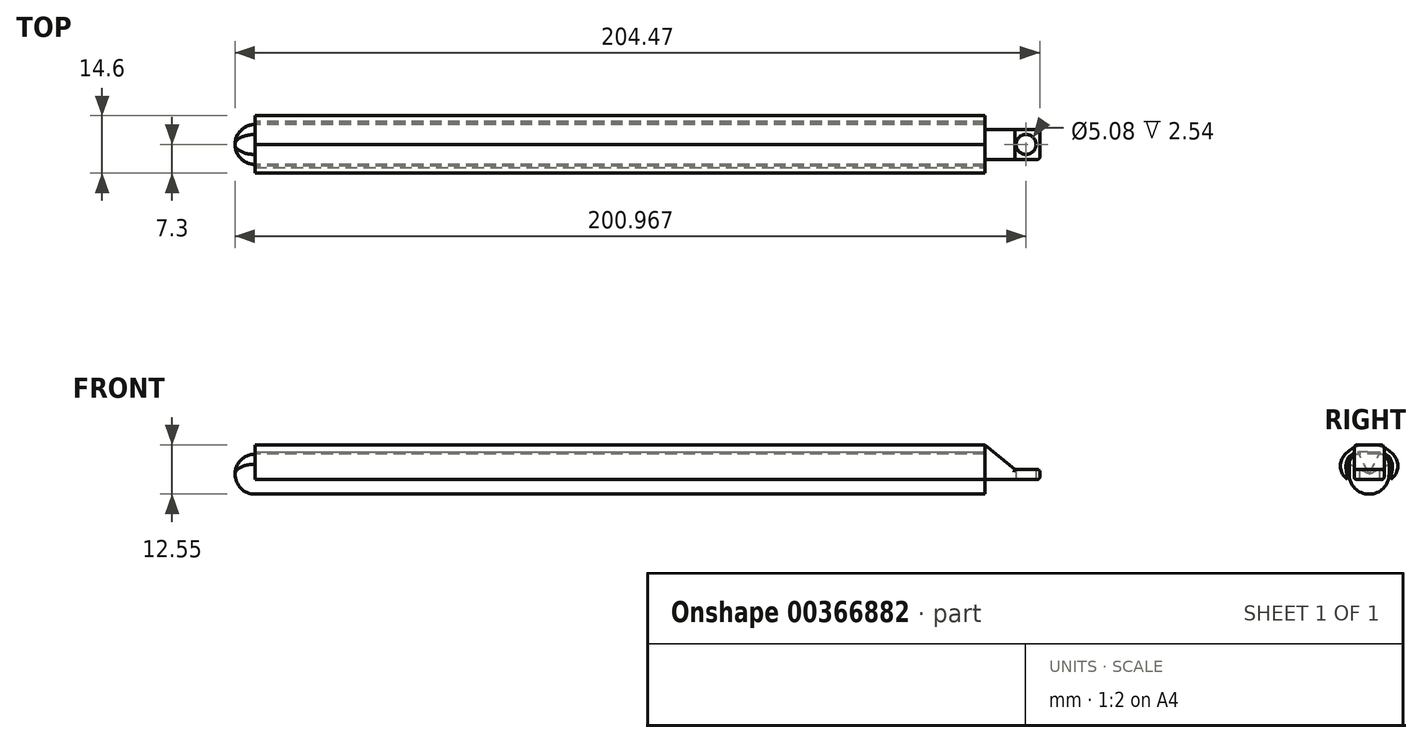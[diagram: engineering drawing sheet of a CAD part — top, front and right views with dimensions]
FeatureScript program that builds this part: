
annotation { "Feature Type Name" : "Feature", "Feature Type Description" : "" }
export const myFeature = defineFeature(function(context is Context, id is Id, definition is map)
    precondition{}
    {
        {
            var Q0;
            Q0=qCreatedBy(makeId("Right.planeOp"),FACE);
            var sketch = newSketch(context, id + "F0", { "sketchPlane" : qUnion([Q0])});
            skLineSegment(sketch, "E0.bottom", {"start": v(2.54, 5.08) * mm, "end": v(-2.54, 5.08) * mm});
            skLineSegment(sketch, "E0.top", {"start": v(0, -5.08) * mm, "end": v(0, -5.08) * mm});
            skLineSegment(sketch, "E0.left", {"start": v(5.08, 2.54) * mm, "end": v(5.08, 0) * mm});
            skLineSegment(sketch, "E0.right", {"start": v(-5.08, 2.54) * mm, "end": v(-5.08, 0) * mm});
            skPoint(sketch, "E0.middle", {"position": v(0, 0) * mm});
            skPoint(sketch, "E1.visualSharp", {"position": v(-5.08, -5.08) * mm});
            skArc(sketch, "E1.filletArc", {"start": v(-5.08, 0) * mm, "mid": v(-3.6, -3.6) * mm, "end": v(0, -5.08) * mm});
            skPoint(sketch, "E2.visualSharp", {"position": v(5.08, -5.08) * mm});
            skArc(sketch, "E2.filletArc", {"start": v(0, -5.08) * mm, "mid": v(3.6, -3.6) * mm, "end": v(5.08, 0) * mm});
            skPoint(sketch, "E3.visualSharp", {"position": v(-5.08, 5.08) * mm});
            skArc(sketch, "E3.filletArc", {"start": v(-2.54, 5.08) * mm, "mid": v(-4.34, 4.34) * mm, "end": v(-5.08, 2.54) * mm});
            skPoint(sketch, "E4.visualSharp", {"position": v(5.08, 5.08) * mm});
            skArc(sketch, "E4.filletArc", {"start": v(5.08, 2.54) * mm, "mid": v(4.34, 4.34) * mm, "end": v(2.54, 5.08) * mm});
            skSolve(sketch);
        }
        {
            var Q0;
            Q0 = qSketchRegion(id + "F0", true);
            extrude(context, id + "F1", {"entities" : qUnion([Q0]), "depth" : 190.5 * mm});
        }
        {
            var Q0;
            Q0=makeQuery(id+"F1.opExtrude","CAP_EDGE",EDGE,{"disambiguationData":[OSD([sQuery(id+"F0.wireOp",EDGE,"E0.bottom")])],"isStart":true});
            fillet(context, id + "F2", {"entities" : qUnion([Q0]), "radius" : 5.08 * mm, "tangentPropagation" : true, "allowEdgeOverflow" : false});
        }
        {
            var Q0;
            Q0=qCreatedBy(makeId("Right.planeOp"),FACE);
            var sketch = newSketch(context, id + "F3", { "sketchPlane" : qUnion([Q0])});
            skFitSpline(sketch, "E5", {"points": [v(0, 7.4) * mm, v(-3.74, 6.75) * mm, v(-7, 3.72) * mm, v(-6.77, 0) * mm, v(-4.67, -1.86) * mm], "startDerivative": vector(-14.81, 2.44) * mm, "endDerivative": vector(10.96, -6.89) * mm});
            skFitSpline(sketch, "E6.MirrorCS", {"points": [v(0, 7.4) * mm, v(3.74, 6.75) * mm, v(7, 3.72) * mm, v(6.77, 0) * mm, v(4.67, -1.86) * mm], "startDerivative": vector(14.81, 2.44) * mm, "endDerivative": vector(-10.96, -6.89) * mm});
            skFitSpline(sketch, "E7", {"points": [v(0, 5.54) * mm, v(2.34, 5.64) * mm, v(4.89, 4.57) * mm, v(5.86, 2.42) * mm, v(5.67, 0) * mm, v(5.47, -1.36) * mm], "startDerivative": vector(11.04, 1.48) * mm, "endDerivative": vector(-1.07, -7.96) * mm});
            skFitSpline(sketch, "E8.MirrorCS", {"points": [v(0, 5.54) * mm, v(-2.34, 5.64) * mm, v(-4.89, 4.57) * mm, v(-5.86, 2.42) * mm, v(-5.67, 0) * mm, v(-5.47, -1.36) * mm], "startDerivative": vector(-11.04, 1.48) * mm, "endDerivative": vector(1.07, -7.96) * mm});
            skSolve(sketch);
        }
        {
            var Q0;
            Q0 = qSketchRegion(id + "F3", true);
            extrude(context, id + "F4", {"entities" : qUnion([Q0]), "depth" : 190.5 * mm});
        }
        {
            var Q0;
            Q0 = qSketchRegion(id + "F3", true);
            extrude(context, id + "F5", {"entities" : qUnion([Q0]), "operationType" : NewBodyOperationType.REMOVE, "depth" : 5.08 * mm});
        }
        {
            var Q0;
            Q0=qCreatedBy(makeId("Front.planeOp"),FACE);
            var sketch = newSketch(context, id + "F6", { "sketchPlane" : qUnion([Q0])});
            skLineSegment(sketch, "E9", {"start": v(190.5, 7.4) * mm, "end": v(190.5, -1.34) * mm});
            skLineSegment(sketch, "E10", {"start": v(190.5, -1.34) * mm, "end": v(198.12, -1.34) * mm});
            skLineSegment(sketch, "E11", {"start": v(198.12, -1.34) * mm, "end": v(198.12, 1.2) * mm});
            skLineSegment(sketch, "E12", {"start": v(198.12, 1.2) * mm, "end": v(190.5, 7.4) * mm});
            skLineSegment(sketch, "E13.bottom", {"start": v(198.12, 1.2) * mm, "end": v(204.47, 1.2) * mm});
            skLineSegment(sketch, "E13.top", {"start": v(198.12, -1.34) * mm, "end": v(204.47, -1.34) * mm});
            skLineSegment(sketch, "E13.left", {"start": v(198.12, 1.2) * mm, "end": v(198.12, -1.34) * mm});
            skLineSegment(sketch, "E13.right", {"start": v(204.47, 1.2) * mm, "end": v(204.47, -1.34) * mm});
            skSolve(sketch);
        }
        {
            var Q0;
            Q0 = qSketchRegion(id + "F6", true);
            extrude(context, id + "F7", {"entities" : qUnion([Q0]), "endBound" : BoundingType.SYMMETRIC, "depth" : 7.62 * mm});
        }
        {
            var Q0;
            Q0=makeQuery(id+"F7.opExtrude","CAP_EDGE",EDGE,{"disambiguationData":[OSD([sQuery(id+"F6.wireOp",EDGE,"E12")])],"isStart":false});
            var Q1;
            Q1=makeQuery(id+"F7.opExtrude","CAP_EDGE",EDGE,{"disambiguationData":[OSD([sQuery(id+"F6.wireOp",EDGE,"E12")])],"isStart":true});
            var Q2;
            Q2=makeQuery(id+"F7.opExtrude","CAP_EDGE",EDGE,{"disambiguationData":[OSD([sQuery(id+"F6.wireOp",EDGE,"E10"),sQuery(id+"F6.wireOp",EDGE,"E13.top")])],"isStart":true});
            var Q3;
            Q3=makeQuery(id+"F7.opExtrude","CAP_EDGE",EDGE,{"disambiguationData":[OSD([sQuery(id+"F6.wireOp",EDGE,"E13.bottom")])],"isStart":true});
            var Q4;
            Q4=makeQuery(id+"F7.opExtrude","CAP_EDGE",EDGE,{"disambiguationData":[OSD([sQuery(id+"F6.wireOp",EDGE,"E13.bottom")])],"isStart":false});
            var Q5;
            Q5=makeQuery(id+"F7.opExtrude","CAP_EDGE",EDGE,{"disambiguationData":[OSD([sQuery(id+"F6.wireOp",EDGE,"E10"),sQuery(id+"F6.wireOp",EDGE,"E13.top")])],"isStart":false});
            var Q6;
            Q6=makeQuery(id+"F7.opExtrude","SWEPT_EDGE",EDGE,{"disambiguationData":[OSD([sQuery(id+"F6.wireOp",EDGE,"E13.bottom"),sQuery(id+"F6.wireOp",EDGE,"E13.right")])]});
            var Q7;
            Q7=makeQuery(id+"F7.opExtrude","SWEPT_EDGE",EDGE,{"disambiguationData":[OSD([sQuery(id+"F6.wireOp",EDGE,"E13.top"),sQuery(id+"F6.wireOp",EDGE,"E13.right")])]});
            var Q8;
            Q8=makeQuery(id+"F7.opExtrude","CAP_EDGE",EDGE,{"disambiguationData":[OSD([sQuery(id+"F6.wireOp",EDGE,"E13.right")])],"isStart":false});
            var Q9;
            Q9=makeQuery(id+"F7.opExtrude","CAP_EDGE",EDGE,{"disambiguationData":[OSD([sQuery(id+"F6.wireOp",EDGE,"E13.right")])],"isStart":true});
            fillet(context, id + "F8", {"entities" : qUnion([Q0, Q1, Q2, Q3, Q4, Q5, Q6, Q7, Q8, Q9]), "radius" : 0.64 * mm, "tangentPropagation" : true, "allowEdgeOverflow" : false});
        }
        {
            var Q0;
            Q0=qCreatedBy(makeId("Top.planeOp"),FACE);
            var sketch = newSketch(context, id + "F9", { "sketchPlane" : qUnion([Q0])});
            skCircle(sketch, "E14", {"center": v(992.04, 0) * mm, "radius": 6.35 * mm});
            skCircle(sketch, "E15", {"center": v(200.97, 0) * mm, "radius": 2.54 * mm});
            skSolve(sketch);
        }
        {
            var Q0;
            Q0 = qSketchRegion(id + "F9", true);
            extrude(context, id + "F10", {"entities" : qUnion([Q0]), "operationType" : NewBodyOperationType.REMOVE, "depth" : 12.7 * mm});
        }
        {
            var Q0;
            Q0 = qSketchRegion(id + "F9", true);
            extrude(context, id + "F11", {"entities" : qUnion([Q0]), "operationType" : NewBodyOperationType.REMOVE, "oppositeDirection" : true, "depth" : 25.4 * mm});
        }
    });
